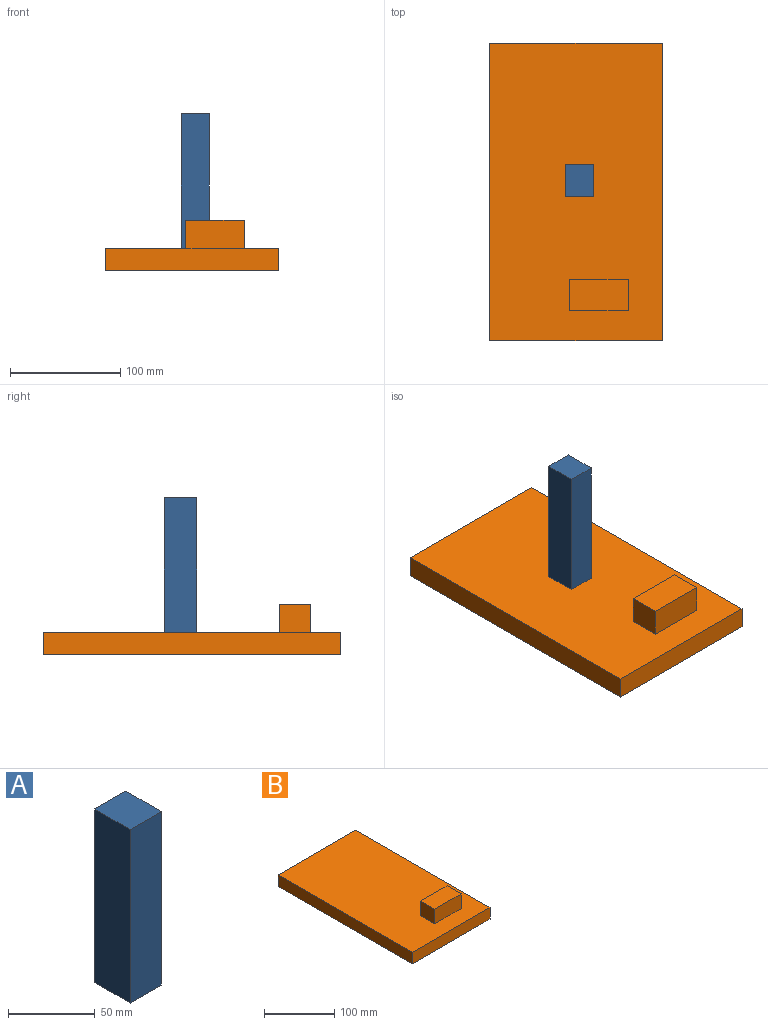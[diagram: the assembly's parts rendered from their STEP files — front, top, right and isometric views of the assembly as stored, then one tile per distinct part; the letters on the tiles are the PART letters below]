
ASSEMBLY  parts=2 mates=1
PART A: 6 faces, bbox 25.4x29.1x122.3 mm
  f0: plane 122.32x25.4mm, normal (0,-1,0), area 3106.9mm2, adj f1,f3,f4,f5
  f1: plane 29.13x25.4mm, normal (0,0,-1), area 740mm2, adj f0,f2,f4,f5
  f2: plane 122.32x25.4mm, normal (0,1,0), area 3106.9mm2, adj f1,f3,f4,f5
  f3: plane 29.13x25.4mm, normal (0,0,1), area 740mm2, adj f0,f2,f4,f5
  f4: plane 122.32x29.13mm, normal (-1,0,0), area 3563.5mm2, adj f0,f1,f2,f3
  f5: plane 122.32x29.13mm, normal (1,0,0), area 3563.5mm2, adj f0,f1,f2,f3
PART B: 77 faces, bbox 156.2x269.5x45.4 mm
  f0: plane 269.52x156.15mm, normal (0,0,1), area 40590.7mm2, adj f1,f2,f3,f4,f72,f73,f74,f75
  f1: plane 269.52x20mm, normal (1,0,0), area 5390.4mm2, adj f0,f2,f4,f5
  f2: plane 156.15x20mm, normal (0,1,0), area 3123.1mm2, adj f0,f1,f3,f5
  f3: plane 269.52x20mm, normal (-1,0,0), area 5390.4mm2, adj f0,f2,f4,f5
  f4: plane 156.15x20mm, normal (0,-1,0), area 3123.1mm2, adj f0,f1,f3,f5
  f5: plane 269.52x156.15mm, normal (0,0,-1), area 20962.7mm2, adj f1,f2,f3,f4,f16,f19,f20,f21
  f6: plane 5x5mm, normal (0,0,1), area 14.1mm2, adj f9,f17,f26,f27,f41,f42,f44
  f7: plane 5x5mm, normal (0,0,1), area 14.1mm2, adj f8,f12,f25,f26,f37,f38,f40
  f8: plane 3x0.5mm, normal (1,0,0), area 1.5mm2, adj f7,f12,f26,f39
  f9: plane 3x0.5mm, normal (-1,0,0), area 1.5mm2, adj f6,f17,f26,f43
  f10: plane 5x5mm, normal (0,0,1), area 14.1mm2, adj f11,f15,f25,f28,f33,f34,f36
  f11: plane 3x0.5mm, normal (0,1,0), area 1.5mm2, adj f10,f15,f25,f35
  f12: plane 3x0.5mm, normal (0,-1,0), area 1.5mm2, adj f7,f8,f25,f39
  f13: plane 5x5mm, normal (0,0,1), area 14.1mm2, adj f14,f18,f27,f28,f29,f30,f32
  f14: plane 3x0.5mm, normal (-1,0,0), area 1.5mm2, adj f13,f18,f28,f31
  f15: plane 3x0.5mm, normal (1,0,0), area 1.5mm2, adj f10,f11,f28,f35
  f16: plane 24x10mm, normal (-1,0,0), area 230.5mm2, adj f5,f21,f47,f49,f54,f70
  f17: plane 3x0.5mm, normal (0,-1,0), area 1.5mm2, adj f6,f9,f27,f43
  f18: plane 3x0.5mm, normal (0,1,0), area 1.5mm2, adj f13,f14,f27,f31
  f19: plane 26.5x10mm, normal (0,-1,0), area 255.5mm2, adj f5,f45,f48,f57,f58,f69
  f20: plane 198x10mm, normal (-1,0,0), area 1980mm2, adj f5,f59,f63,f65
  f21: plane 26.5x10mm, normal (0,-1,0), area 255.5mm2, adj f5,f16,f47,f56,f63,f70
  f22: plane 198x10mm, normal (1,0,0), area 1980mm2, adj f5,f57,f62,f67
  f23: plane 98x10mm, normal (0,1,0), area 980mm2, adj f5,f61,f65,f67
  f24: plane 223x98mm, normal (0,0,-1), area 2335.3mm2, adj f25,f26,f27,f28,f29,f30,f32,f33
  f25: plane 194x11mm, normal (1,0,0), area 2116mm2, adj f7,f10,f11,f12,f24,f26,f28,f33
  f26: plane 94x11mm, normal (0,-1,0), area 1016mm2, adj f6,f7,f8,f9,f24,f25,f27,f38
  f27: plane 194x11mm, normal (-1,0,0), area 2116mm2, adj f6,f13,f17,f18,f24,f26,f28,f29
  f28: plane 94x11mm, normal (0,1,0), area 1016mm2, adj f10,f13,f14,f15,f24,f25,f27,f30
  f29: plane 2x1.5mm, normal (0,1,0), area 3mm2, adj f13,f24,f27,f32
  f30: plane 2x1.5mm, normal (-1,0,0), area 3mm2, adj f13,f24,f28,f32
  f31: plane 3x3mm, normal (0,0,1), area 9mm2, adj f14,f18,f27,f28
  f32: cylinder r=3mm len=3mm, axis (0,0,1), area 7.1mm2, adj f13,f24,f29,f30
  f33: plane 2x1.5mm, normal (0,1,0), area 3mm2, adj f10,f24,f25,f36
  f34: plane 2x1.5mm, normal (1,0,0), area 3mm2, adj f10,f24,f28,f36
  f35: plane 3x3mm, normal (0,0,1), area 9mm2, adj f11,f15,f25,f28
  f36: cylinder r=3mm len=3mm, axis (0,0,1), area 7.1mm2, adj f10,f24,f33,f34
  f37: plane 2x1.5mm, normal (0,-1,0), area 3mm2, adj f7,f24,f25,f40
  f38: plane 2x1.5mm, normal (1,0,0), area 3mm2, adj f7,f24,f26,f40
  f39: plane 3x3mm, normal (0,0,1), area 9mm2, adj f8,f12,f25,f26
  f40: cylinder r=3mm len=3mm, axis (0,0,1), area 7.1mm2, adj f7,f24,f37,f38
  f41: plane 2x1.5mm, normal (-1,0,0), area 3mm2, adj f6,f24,f26,f44
  f42: plane 2x1.5mm, normal (0,-1,0), area 3mm2, adj f6,f24,f27,f44
  f43: plane 3x3mm, normal (0,0,1), area 9mm2, adj f9,f17,f26,f27
  f44: cylinder r=3mm len=3mm, axis (0,0,1), area 7.1mm2, adj f6,f24,f41,f42
  f45: plane 24x10mm, normal (1,0,0), area 230.5mm2, adj f5,f19,f48,f50,f55,f69
  f46: plane 43x10mm, normal (0,-1,0), area 430mm2, adj f5,f49,f50,f51
  f47: cylinder r=1mm len=9.5mm, axis (0,0,1), area 14.9mm2, adj f5,f16,f21,f70
  f48: cylinder r=1mm len=9.5mm, axis (0,0,1), area 14.9mm2, adj f5,f19,f45,f69
  f49: cylinder r=1mm len=10mm, axis (0,0,1), area 15.7mm2, adj f5,f16,f46,f52
  f50: cylinder r=1mm len=10mm, axis (0,0,1), area 15.7mm2, adj f5,f45,f46,f53
  f51: cylinder r=1mm len=43mm, axis (1,0,0), area 67.5mm2, adj f24,f46,f52,f53
  f52: sphere r=1mm, area 1.6mm2, adj f49,f51,f54
  f53: sphere r=1mm, area 1.6mm2, adj f50,f51,f55
  f54: cylinder r=1mm len=25mm, axis (0,-1,0), area 38.3mm2, adj f16,f24,f52,f56
  f55: cylinder r=1mm len=25mm, axis (0,1,0), area 38.3mm2, adj f24,f45,f53,f58
  f56: cylinder r=1mm len=27.5mm, axis (-1,0,0), area 42.2mm2, adj f21,f24,f54,f64
  f57: cylinder r=1mm len=10mm, axis (0,0,-1), area 15.7mm2, adj f5,f19,f22,f60
  f58: cylinder r=1mm len=27.5mm, axis (-1,0,0), area 42.2mm2, adj f19,f24,f55,f60
  f59: cylinder r=1mm len=198mm, axis (0,1,0), area 311mm2, adj f20,f24,f64,f66
  f60: sphere r=1mm, area 1.6mm2, adj f57,f58,f62
  f61: cylinder r=1mm len=98mm, axis (1,0,0), area 153.9mm2, adj f23,f24,f66,f68
  f62: cylinder r=1mm len=198mm, axis (0,-1,0), area 311mm2, adj f22,f24,f60,f68
  f63: cylinder r=1mm len=10mm, axis (0,0,-1), area 15.7mm2, adj f5,f20,f21,f64
  f64: sphere r=1mm, area 1.6mm2, adj f56,f59,f63
  f65: cylinder r=1mm len=10mm, axis (0,0,-1), area 15.7mm2, adj f5,f20,f23,f66
  f66: sphere r=1mm, area 1.6mm2, adj f59,f61,f65
  f67: cylinder r=1mm len=10mm, axis (0,0,-1), area 15.7mm2, adj f5,f22,f23,f68
  f68: sphere r=1mm, area 1.6mm2, adj f61,f62,f67
  f69: plane 1x1mm, normal (0,0,-1), area 0.2mm2, adj f19,f45,f48
  f70: plane 1x1mm, normal (0,0,-1), area 0.2mm2, adj f16,f21,f47
  f71: plane 194x94mm, normal (0,0,-1), area 18236mm2, adj f25,f26,f27,f28
  f72: plane 52.97x25.4mm, normal (0,1,0), area 1345.3mm2, adj f0,f73,f75,f76
  f73: plane 28.25x25.4mm, normal (-1,0,0), area 717.5mm2, adj f0,f72,f74,f76
  f74: plane 52.97x25.4mm, normal (0,-1,0), area 1345.3mm2, adj f0,f73,f75,f76
  f75: plane 28.25x25.4mm, normal (1,0,0), area 717.5mm2, adj f0,f72,f74,f76
  f76: plane 52.97x28.25mm, normal (0,0,1), area 1496.2mm2, adj f72,f73,f74,f75
PLACE A t=(-151.47,-17.46,-62.05)mm
PLACE B t=(-88.87,-13.37,-62.05)mm
MATE planar A.f1 <-> B.f0  axis (0,0,-1) through (-86.98,-1.42,-41.05)mm
